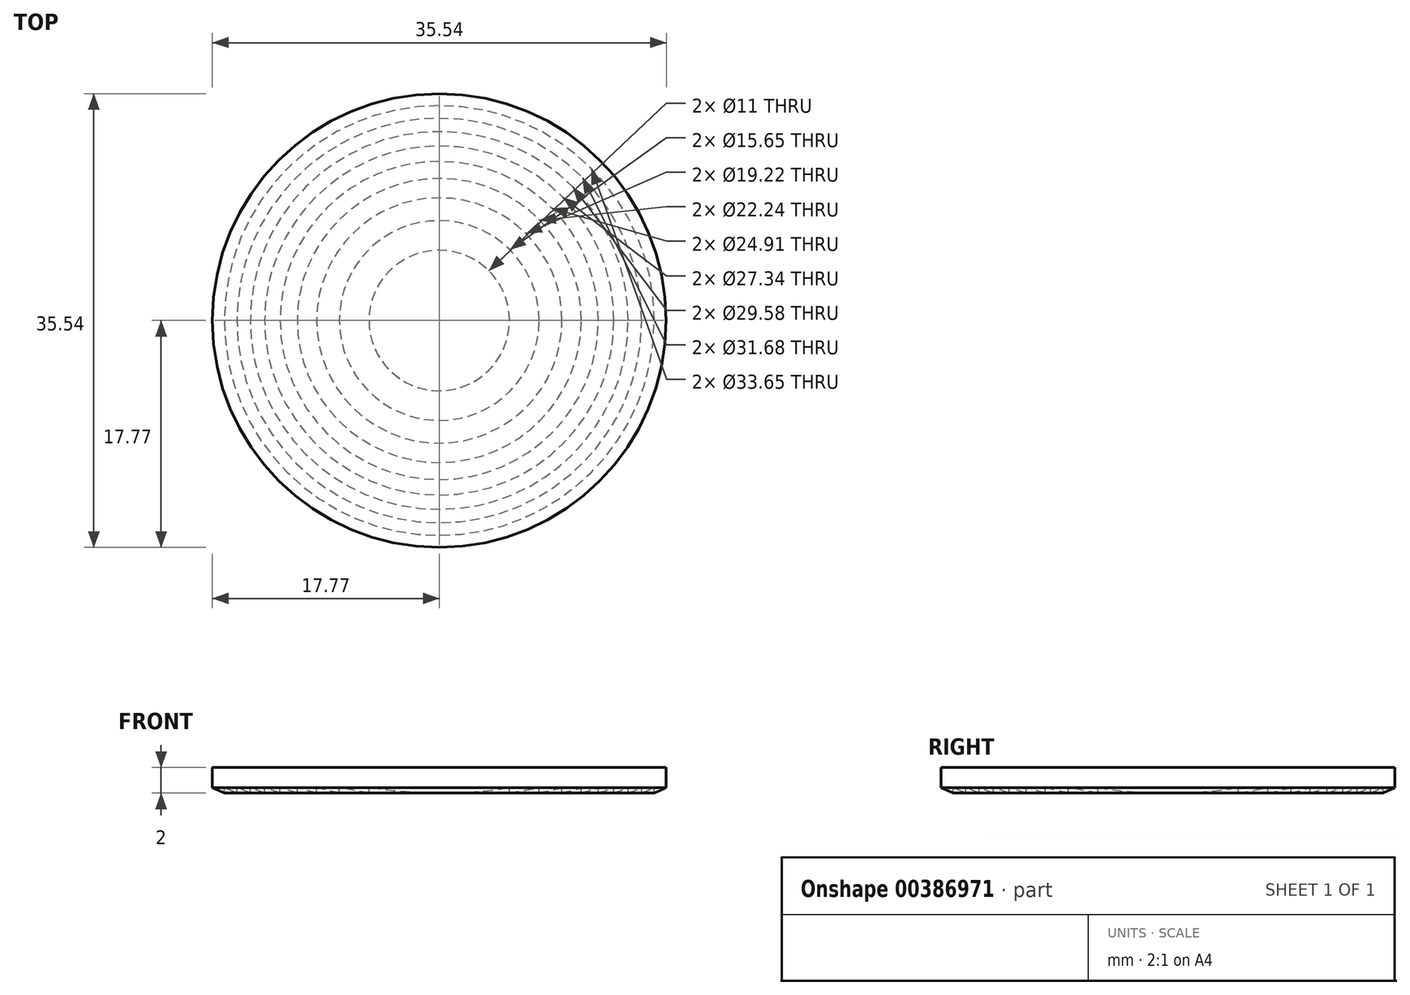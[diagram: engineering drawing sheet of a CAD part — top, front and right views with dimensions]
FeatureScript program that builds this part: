
annotation { "Feature Type Name" : "Feature", "Feature Type Description" : "" }
export const myFeature = defineFeature(function(context is Context, id is Id, definition is map)
    precondition{}
    {
        {
            var Q0;
            Q0=qCreatedBy(makeId("Front.planeOp"),FACE);
            var sketch = newSketch(context, id + "F0", { "sketchPlane" : qUnion([Q0])});
            skLineSegment(sketch, "E0", {"start": v(5.5, -37.58) * mm, "end": v(0, -37.58) * mm});
            skLineSegment(sketch, "E1", {"start": v(0, -37.58) * mm, "end": v(0, -38.01) * mm});
            skLineSegment(sketch, "E2", {"start": v(0, -37.58) * mm, "end": v(-5.5, -37.58) * mm});
            skArc(sketch, "E3", {"start": v(-5.5, -37.58) * mm, "mid": v(0, -38.01) * mm, "end": v(5.5, -37.58) * mm});
            skLineSegment(sketch, "E4", {"start": v(5.5, -37.58) * mm, "end": v(7.82, -37.58) * mm});
            skLineSegment(sketch, "E5", {"start": v(5.5, -37.58) * mm, "end": v(5.5, -38.01) * mm});
            skLineSegment(sketch, "E6", {"start": v(5.5, -38.01) * mm, "end": v(7.82, -37.58) * mm});
            skLineSegment(sketch, "E7", {"start": v(7.82, -37.58) * mm, "end": v(7.82, -38.01) * mm});
            skLineSegment(sketch, "E8", {"start": v(9.6, -37.58) * mm, "end": v(9.6, -38.01) * mm});
            skLineSegment(sketch, "E9", {"start": v(9.6, -37.58) * mm, "end": v(7.82, -37.58) * mm});
            skLineSegment(sketch, "E10", {"start": v(9.6, -37.58) * mm, "end": v(11.12, -37.58) * mm});
            skLineSegment(sketch, "E11", {"start": v(11.12, -37.58) * mm, "end": v(11.12, -38.01) * mm});
            skLineSegment(sketch, "E12", {"start": v(11.12, -37.58) * mm, "end": v(12.46, -37.58) * mm});
            skLineSegment(sketch, "E13", {"start": v(12.46, -37.58) * mm, "end": v(12.46, -38.01) * mm});
            skLineSegment(sketch, "E14", {"start": v(12.46, -37.58) * mm, "end": v(13.67, -37.58) * mm});
            skLineSegment(sketch, "E15", {"start": v(13.67, -37.58) * mm, "end": v(13.67, -38.01) * mm});
            skLineSegment(sketch, "E16", {"start": v(13.67, -37.58) * mm, "end": v(14.8, -37.58) * mm});
            skLineSegment(sketch, "E17", {"start": v(14.8, -37.58) * mm, "end": v(14.8, -38.01) * mm});
            skLineSegment(sketch, "E18", {"start": v(14.8, -37.58) * mm, "end": v(15.84, -37.58) * mm});
            skLineSegment(sketch, "E19", {"start": v(15.84, -37.58) * mm, "end": v(16.83, -37.58) * mm});
            skLineSegment(sketch, "E20", {"start": v(15.84, -37.58) * mm, "end": v(15.84, -38.01) * mm});
            skLineSegment(sketch, "E21", {"start": v(16.83, -37.58) * mm, "end": v(16.83, -38.01) * mm});
            skLineSegment(sketch, "E22", {"start": v(16.83, -37.58) * mm, "end": v(17.77, -37.58) * mm});
            skLineSegment(sketch, "E23", {"start": v(7.82, -38.01) * mm, "end": v(9.6, -37.58) * mm});
            skLineSegment(sketch, "E24", {"start": v(9.6, -38.01) * mm, "end": v(11.12, -37.58) * mm});
            skLineSegment(sketch, "E25", {"start": v(11.12, -38.01) * mm, "end": v(12.46, -37.58) * mm});
            skLineSegment(sketch, "E26", {"start": v(12.46, -38.01) * mm, "end": v(13.67, -37.58) * mm});
            skLineSegment(sketch, "E27", {"start": v(13.67, -38.01) * mm, "end": v(14.8, -37.58) * mm});
            skLineSegment(sketch, "E28", {"start": v(14.8, -38.01) * mm, "end": v(15.84, -37.58) * mm});
            skLineSegment(sketch, "E29", {"start": v(15.84, -38.01) * mm, "end": v(16.83, -37.58) * mm});
            skLineSegment(sketch, "E30", {"start": v(16.83, -38.01) * mm, "end": v(17.77, -37.58) * mm});
            skLineSegment(sketch, "E31", {"start": v(0, -37.58) * mm, "end": v(0, -36.01) * mm});
            skLineSegment(sketch, "E32", {"start": v(17.77, -37.58) * mm, "end": v(17.77, -36.01) * mm});
            skLineSegment(sketch, "E33", {"start": v(17.77, -36.01) * mm, "end": v(0, -36.01) * mm});
            skSolve(sketch);
        }
        {
            var Q0;
            {var subQ0=sQuery(id+"F0.wireOp",EDGE,"E0");Q0=makeQuery(id+"F0.imprint","IMPRINT",FACE,{"disambiguationData":[TD([[makeQuery(id+"F0.imprint","IMPRINT",EDGE,{"derivedFrom":subQ0}),1.0]])]});}
            var Q1;
            Q1=makeQuery(id+"F0.imprint","IMPRINT",FACE,{"disambiguationData":[TD([[makeQuery(id+"F0.imprint","IMPRINT",EDGE,{"derivedFrom":sQuery(id+"F0.wireOp",EDGE,"E4")}),-1.0]])]});
            var Q2;
            Q2=makeQuery(id+"F0.imprint","IMPRINT",FACE,{"disambiguationData":[TD([[makeQuery(id+"F0.imprint","IMPRINT",EDGE,{"derivedFrom":sQuery(id+"F0.wireOp",EDGE,"E7")}),1.0]])]});
            var Q3;
            Q3=makeQuery(id+"F0.imprint","IMPRINT",FACE,{"disambiguationData":[TD([[makeQuery(id+"F0.imprint","IMPRINT",EDGE,{"derivedFrom":sQuery(id+"F0.wireOp",EDGE,"E8")}),1.0]])]});
            var Q4;
            Q4=makeQuery(id+"F0.imprint","IMPRINT",FACE,{"disambiguationData":[TD([[makeQuery(id+"F0.imprint","IMPRINT",EDGE,{"derivedFrom":sQuery(id+"F0.wireOp",EDGE,"E11")}),1.0]])]});
            var Q5;
            Q5=makeQuery(id+"F0.imprint","IMPRINT",FACE,{"disambiguationData":[TD([[makeQuery(id+"F0.imprint","IMPRINT",EDGE,{"derivedFrom":sQuery(id+"F0.wireOp",EDGE,"E13")}),1.0]])]});
            var Q6;
            Q6=makeQuery(id+"F0.imprint","IMPRINT",FACE,{"disambiguationData":[TD([[makeQuery(id+"F0.imprint","IMPRINT",EDGE,{"derivedFrom":sQuery(id+"F0.wireOp",EDGE,"E15")}),1.0]])]});
            var Q7;
            Q7=makeQuery(id+"F0.imprint","IMPRINT",FACE,{"disambiguationData":[TD([[makeQuery(id+"F0.imprint","IMPRINT",EDGE,{"derivedFrom":sQuery(id+"F0.wireOp",EDGE,"E17")}),1.0]])]});
            var Q8;
            Q8=makeQuery(id+"F0.imprint","IMPRINT",FACE,{"disambiguationData":[TD([[makeQuery(id+"F0.imprint","IMPRINT",EDGE,{"derivedFrom":sQuery(id+"F0.wireOp",EDGE,"E19")}),-1.0]])]});
            var Q9;
            Q9=makeQuery(id+"F0.imprint","IMPRINT",FACE,{"disambiguationData":[TD([[makeQuery(id+"F0.imprint","IMPRINT",EDGE,{"derivedFrom":sQuery(id+"F0.wireOp",EDGE,"E21")}),1.0]])]});
            var Q10;
            Q10=makeQuery(id+"F0.imprint","IMPRINT",FACE,{"disambiguationData":[TD([[makeQuery(id+"F0.imprint","IMPRINT",EDGE,{"derivedFrom":sQuery(id+"F0.wireOp",EDGE,"E0")}),-1.0]])]});
            var Q11;
            Q11=sQuery(id+"F0.wireOp",EDGE,"E1");
            revolve(context, id + "F1", {"entities" : qUnion([Q0, Q1, Q2, Q3, Q4, Q5, Q6, Q7, Q8, Q9, Q10]), "axis" : qUnion([Q11]), "revolveType" : RevolveType.FULL});
        }
    });
